# Revit family: DC_Holyoake_MEQ_RLHL_13
name_source: partatom
category: Air Terminals
revit_build: Autodesk Revit 2014 (Build: 20130308_1515(x64)
units: mm (PartAtom-declared; Revit-internal decimal feet)

## types (1)
- DC_Holyoake_MEQ_RLHL_13
    Act Louver Number = 29
    Blade Length = 158 mm
    Calc Length = 175 mm  [stored 0.574147 ft]
    Calc Width = 600 mm  [stored 1.9685 ft]
    Depth = 32 mm  [stored 0.104987 ft]
    Holyoake Product Range = Holyoake Exhaust and Return Grilles
    Length = 100 mm  [stored 0.328084 ft]
    Manufacturer = Holyoake
    Material-Body = Holyoake White
    Max Flow = 3200.0 L/s
    Min Flow = 20.0 L/s
    Model = Holyoake RLHL
    Noise Level NC Max = 60
    Noise Level NC Min = 10
    Static Pressure Max = 31.0 Pa
    Static Pressure Min = 3.0 Pa
    URL = www.holyoake.com.au
    Width = 600 mm  [stored 1.9685 ft]

note: [stored X ft] marks values corroborated as IEEE doubles in the binary element streams (Revit-internal decimal feet)

## geometry (parser evidence)
native form markers: Blend x4, Sweep x8
no freeform markers — native parametric forms only
